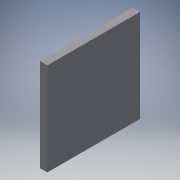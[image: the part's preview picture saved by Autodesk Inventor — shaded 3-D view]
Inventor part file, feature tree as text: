
AUTODESK INVENTOR PART (.ipt)
format: ipt  version: 2017 (Build 210142000, 142)  size: 88,064 bytes
history: native  units: in
note: dims shown in document units (in); Inventor stores cm internally (conversion verified against a paired STEP export)
features: extrude x1, sketch x1
ambient origin geometry x8: Origin, YZ Plane, XZ Plane, XY Plane, X Axis, Y Axis, Z Axis, Center Point
bodies: Solid1 (feature_tree)
feature tree (2):
  extrude  "Extrusion1"  Depth=39.3701in
  sketch  "Sketch1"  dims[d0=39.3701in d1=39.3701in d2=3.1496in d3=0.0in]
